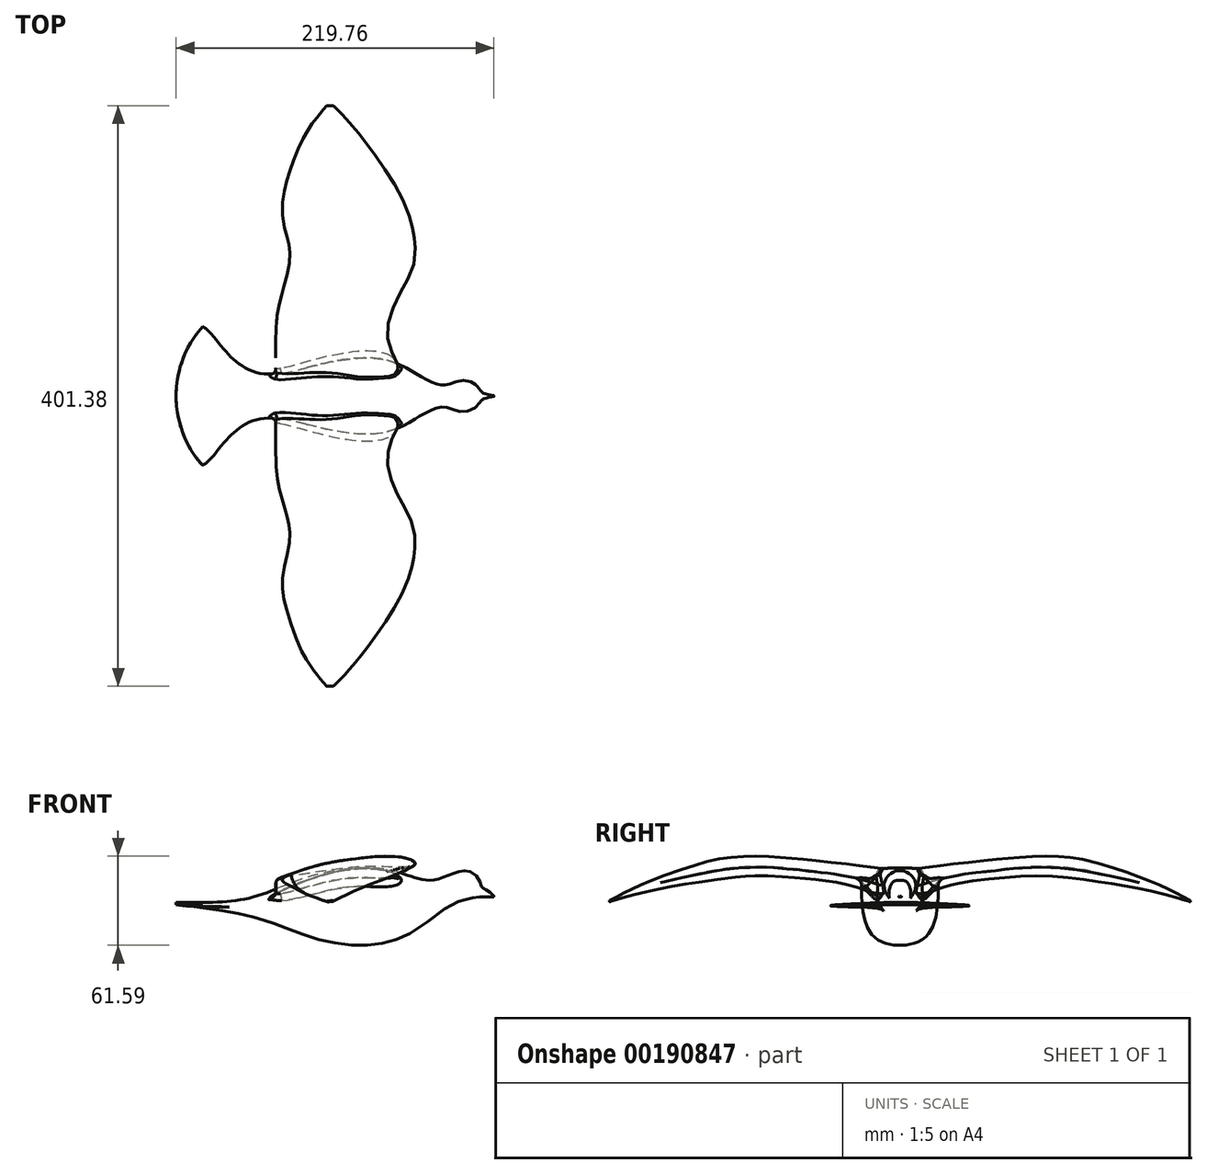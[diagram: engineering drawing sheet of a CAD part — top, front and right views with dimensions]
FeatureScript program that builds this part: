
annotation { "Feature Type Name" : "Feature", "Feature Type Description" : "" }
export const myFeature = defineFeature(function(context is Context, id is Id, definition is map)
    precondition{}
    {
        {
            var Q0;
            Q0=qCreatedBy(makeId("Front.planeOp"),FACE);
            var sketch = newSketch(context, id + "F0", { "sketchPlane" : qUnion([Q0])});
            skFitSpline(sketch, "E0", {"points": [v(88.88, 8.24) * mm, v(81.16, 14.04) * mm, v(79.82, 15.6) * mm, v(77.74, 20.52) * mm, v(69.16, 26.32) * mm, v(49.8, 20.45) * mm, v(34.16, 21.33) * mm, v(13, 27.34) * mm, v(-24.47, 25.74) * mm, v(-55.86, 16.14) * mm, v(-89.32, 5.77) * mm, v(-146.84, 4.8) * mm], "startDerivative": vector(-94.93, 149.18) * mm, "endDerivative": vector(-242.05, 4.9) * mm});
            skFitSpline(sketch, "E1", {"points": [v(-146.84, 4.8) * mm, v(-98.32, -1.47) * mm, v(-63.3, -10.47) * mm, v(-28.78, -22.29) * mm, v(10.92, -24.11) * mm, v(36.51, -13.67) * mm, v(49.57, -3.48) * mm, v(62.2, 4.2) * mm, v(74.07, 7.48) * mm, v(79.66, 8.19) * mm, v(88.88, 8.24) * mm], "startDerivative": vector(194.97, -32.1) * mm, "endDerivative": vector(155.18, 5.35) * mm});
            skLineSegment(sketch, "E2", {"start": v(78.61, 8.13) * mm, "end": v(80.27, 14.79) * mm, "construction": true});
            skLineSegment(sketch, "E3", {"start": v(70.02, 6.63) * mm, "end": v(70.7, 26.08) * mm, "construction": true});
            skLineSegment(sketch, "E4", {"start": v(58.33, 2.37) * mm, "end": v(51.98, 21.1) * mm, "construction": true});
            skLineSegment(sketch, "E5", {"start": v(29.9, -17.56) * mm, "end": v(25.63, 24.14) * mm, "construction": true});
            skLineSegment(sketch, "E6", {"start": v(-8, -25.25) * mm, "end": v(-11.3, 27.63) * mm, "construction": true});
            skLineSegment(sketch, "E7", {"start": v(-48.68, -15.99) * mm, "end": v(-48.68, 18.9) * mm, "construction": true});
            skLineSegment(sketch, "E8", {"start": v(-78.1, -5.74) * mm, "end": v(-78.1, 8.02) * mm, "construction": true});
            skLineSegment(sketch, "E9", {"start": v(-99.16, -1.33) * mm, "end": v(-99.57, 4.76) * mm, "construction": true});
            skLineSegment(sketch, "E10", {"start": v(88.2, 8.22) * mm, "end": v(88.46, 8.84) * mm});
            skLineSegment(sketch, "E11", {"start": v(-133.72, 3.08) * mm, "end": v(-133.72, 4.45) * mm});
            skLineSegment(sketch, "E12", {"start": v(-116.16, 4.23) * mm, "end": v(-116.16, 1) * mm, "construction": true});
            skLineSegment(sketch, "E13", {"start": v(-137.67, 4.56) * mm, "end": v(-133.72, 4.45) * mm});
            skLineSegment(sketch, "E14", {"start": v(-137.8, 3.61) * mm, "end": v(-133.72, 3.08) * mm});
            skLineSegment(sketch, "E15", {"start": v(-137.67, 4.56) * mm, "end": v(-137.8, 3.61) * mm});
            skSolve(sketch);
        }
        {
            var Q0;
            Q0=sQuery(id+"F0.wireOp",EDGE,"E10");
            cPlane(context, id + "F1", {"entities" : qUnion([Q0]), "cplaneType" : CPlaneType.LINE_ANGLE, "offset" : 25 * mm, "angle" : 0 * degree, "width" : 150 * mm, "height" : 150 * mm});
        }
        {
            var Q0;
            Q0=qCreatedBy(id+"F1.planeOp",FACE);
            var sketch = newSketch(context, id + "F2", { "sketchPlane" : qUnion([Q0])});
            skPoint(sketch, "E16.0", {"position": v(0, 41.6) * mm});
            skFitSpline(sketch, "E17", {"points": [v(0, 41.93) * mm, v(-0.33, 41.79) * mm, v(-0.34, 41.48) * mm, v(0, 41.26) * mm], "startDerivative": vector(-1.4, 0) * mm, "endDerivative": vector(1.32, 0) * mm});
            skFitSpline(sketch, "E18.MirrorCS", {"points": [v(0, 41.93) * mm, v(0.33, 41.79) * mm, v(0.34, 41.48) * mm, v(0, 41.26) * mm], "startDerivative": vector(1.4, 0) * mm, "endDerivative": vector(-1.32, 0) * mm});
            skSolve(sketch);
        }
        {
            var Q0;
            Q0=sQuery(id+"F0.wireOp",EDGE,"E2");
            cPlane(context, id + "F3", {"entities" : qUnion([Q0]), "cplaneType" : CPlaneType.LINE_ANGLE, "offset" : 25 * mm, "angle" : 0 * degree, "width" : 150 * mm, "height" : 150 * mm});
        }
        {
            var Q0;
            Q0=qCreatedBy(id+"F3.planeOp",FACE);
            var sketch = newSketch(context, id + "F4", { "sketchPlane" : qUnion([Q0])});
            skFitSpline(sketch, "E19", {"points": [v(0, 33.77) * mm, v(-2.62, 32.5) * mm, v(-2.94, 28.5) * mm, v(0, 26.91) * mm], "startDerivative": vector(-11.48, 0) * mm, "endDerivative": vector(10.21, 0) * mm});
            skFitSpline(sketch, "E20.MirrorCS", {"points": [v(0, 33.77) * mm, v(2.62, 32.5) * mm, v(2.94, 28.5) * mm, v(0, 26.91) * mm], "startDerivative": vector(11.48, 0) * mm, "endDerivative": vector(-10.21, 0) * mm});
            skSolve(sketch);
        }
        {
            var Q0;
            Q0=sQuery(id+"F0.wireOp",EDGE,"E3");
            cPlane(context, id + "F5", {"entities" : qUnion([Q0]), "cplaneType" : CPlaneType.LINE_ANGLE, "offset" : 25 * mm, "angle" : 0 * degree, "width" : 150 * mm, "height" : 150 * mm});
        }
        {
            var Q0;
            Q0=qCreatedBy(id+"F5.planeOp",FACE);
            var sketch = newSketch(context, id + "F6", { "sketchPlane" : qUnion([Q0])});
            skFitSpline(sketch, "E21", {"points": [v(0, 28.5) * mm, v(-9.3, 23.37) * mm, v(-8.68, 12.9) * mm, v(0, 9.03) * mm], "startDerivative": vector(-26.88, 0) * mm, "endDerivative": vector(31.08, 0) * mm});
            skFitSpline(sketch, "E22.MirrorCS", {"points": [v(0, 28.5) * mm, v(9.3, 23.37) * mm, v(8.68, 12.9) * mm, v(0, 9.03) * mm], "startDerivative": vector(26.88, 0) * mm, "endDerivative": vector(-31.08, 0) * mm});
            skSolve(sketch);
        }
        {
            var Q0;
            Q0=sQuery(id+"F0.wireOp",EDGE,"E4");
            cPlane(context, id + "F7", {"entities" : qUnion([Q0]), "cplaneType" : CPlaneType.LINE_ANGLE, "offset" : 25 * mm, "angle" : 0 * degree, "width" : 150 * mm, "height" : 150 * mm});
        }
        {
            var Q0;
            Q0=qCreatedBy(id+"F7.planeOp",FACE);
            var sketch = newSketch(context, id + "F8", { "sketchPlane" : qUnion([Q0])});
            skFitSpline(sketch, "E23", {"points": [v(0, 3.3) * mm, v(-6.8, -1.95) * mm, v(-7.06, -11.7) * mm, v(0, -16.48) * mm], "startDerivative": vector(-36.57, 0) * mm, "endDerivative": vector(34.27, 0) * mm});
            skFitSpline(sketch, "E24.MirrorCS", {"points": [v(0, 3.3) * mm, v(6.8, -1.95) * mm, v(7.06, -11.7) * mm, v(0, -16.48) * mm], "startDerivative": vector(36.57, 0) * mm, "endDerivative": vector(-34.27, 0) * mm});
            skSolve(sketch);
        }
        {
            var Q0;
            Q0=sQuery(id+"F0.wireOp",EDGE,"E5");
            cPlane(context, id + "F9", {"entities" : qUnion([Q0]), "cplaneType" : CPlaneType.LINE_ANGLE, "offset" : 25 * mm, "angle" : 0 * degree, "width" : 150 * mm, "height" : 150 * mm});
        }
        {
            var Q0;
            Q0=qCreatedBy(id+"F9.planeOp",FACE);
            var sketch = newSketch(context, id + "F10", { "sketchPlane" : qUnion([Q0])});
            skFitSpline(sketch, "E25", {"points": [v(0, 21.4) * mm, v(-14.3, 18.7) * mm, v(-19.1, 14.04) * mm, v(-15, -12.2) * mm, v(0, -20.5) * mm], "startDerivative": vector(-90.7, 0) * mm, "endDerivative": vector(69.38, 0) * mm});
            skFitSpline(sketch, "E26.MirrorCS", {"points": [v(0, 21.4) * mm, v(14.3, 18.7) * mm, v(19.1, 14.04) * mm, v(15, -12.2) * mm, v(0, -20.5) * mm], "startDerivative": vector(90.7, 0) * mm, "endDerivative": vector(-69.38, 0) * mm});
            skSolve(sketch);
        }
        {
            var Q0;
            Q0=sQuery(id+"F0.wireOp",EDGE,"E6");
            cPlane(context, id + "F11", {"entities" : qUnion([Q0]), "cplaneType" : CPlaneType.LINE_ANGLE, "offset" : 25 * mm, "angle" : 0 * degree, "width" : 150 * mm, "height" : 150 * mm});
        }
        {
            var Q0;
            Q0=qCreatedBy(id+"F11.planeOp",FACE);
            var sketch = newSketch(context, id + "F12", { "sketchPlane" : qUnion([Q0])});
            skFitSpline(sketch, "E27", {"points": [v(0, 28.28) * mm, v(-20, 26.45) * mm, v(-24.93, 24.12) * mm, v(-25.49, 20.68) * mm, v(-21, -15.24) * mm, v(0, -24.7) * mm], "startDerivative": vector(-91.64, 0) * mm, "endDerivative": vector(71.43, 0) * mm});
            skFitSpline(sketch, "E28.MirrorCS", {"points": [v(0, 28.28) * mm, v(20, 26.45) * mm, v(24.93, 24.12) * mm, v(25.49, 20.68) * mm, v(21, -15.24) * mm, v(0, -24.7) * mm], "startDerivative": vector(91.64, 0) * mm, "endDerivative": vector(-71.43, 0) * mm});
            skSolve(sketch);
        }
        {
            var Q0;
            Q0=sQuery(id+"F0.wireOp",EDGE,"E7");
            cPlane(context, id + "F13", {"entities" : qUnion([Q0]), "cplaneType" : CPlaneType.LINE_ANGLE, "offset" : 25 * mm, "angle" : 0 * degree, "width" : 150 * mm, "height" : 150 * mm});
        }
        {
            var Q0;
            Q0=qCreatedBy(id+"F13.planeOp",FACE);
            var sketch = newSketch(context, id + "F14", { "sketchPlane" : qUnion([Q0])});
            skFitSpline(sketch, "E29", {"points": [v(0, 18.9) * mm, v(-14, 16.03) * mm, v(-17.48, 14.36) * mm, v(-17.75, 10.54) * mm, v(-13.32, -9.87) * mm, v(0, -15.99) * mm], "startDerivative": vector(-44.92, 0) * mm, "endDerivative": vector(32.23, 0) * mm});
            skFitSpline(sketch, "E30.MirrorCS", {"points": [v(0, 18.9) * mm, v(14, 16.03) * mm, v(17.48, 14.36) * mm, v(17.75, 10.54) * mm, v(13.32, -9.87) * mm, v(0, -15.99) * mm], "startDerivative": vector(44.92, 0) * mm, "endDerivative": vector(-32.23, 0) * mm});
            skSolve(sketch);
        }
        {
            var Q0;
            Q0=sQuery(id+"F0.wireOp",EDGE,"E8");
            cPlane(context, id + "F15", {"entities" : qUnion([Q0]), "cplaneType" : CPlaneType.LINE_ANGLE, "offset" : 25 * mm, "angle" : 0 * degree, "width" : 150 * mm, "height" : 150 * mm});
        }
        {
            var Q0;
            Q0=qCreatedBy(id+"F15.planeOp",FACE);
            var sketch = newSketch(context, id + "F16", { "sketchPlane" : qUnion([Q0])});
            skFitSpline(sketch, "E31.MirrorCS", {"points": [v(0, 8.02) * mm, v(12.6, 5.46) * mm, v(17.04, 3.17) * mm, v(12.95, -0.34) * mm, v(0, -5.74) * mm], "startDerivative": vector(27.61, 0) * mm, "endDerivative": vector(-43.83, 0) * mm});
            skFitSpline(sketch, "E32.MirrorCS", {"points": [v(0, 8.02) * mm, v(-12.6, 5.46) * mm, v(-17.04, 3.17) * mm, v(-12.95, -0.34) * mm, v(0, -5.74) * mm], "startDerivative": vector(-27.61, 0) * mm, "endDerivative": vector(43.83, 0) * mm});
            skSolve(sketch);
        }
        {
            var Q0;
            Q0=sQuery(id+"F0.wireOp",EDGE,"E9");
            cPlane(context, id + "F17", {"entities" : qUnion([Q0]), "cplaneType" : CPlaneType.LINE_ANGLE, "offset" : 25 * mm, "angle" : 0 * degree, "width" : 150 * mm, "height" : 150 * mm});
        }
        {
            var Q0;
            Q0=qCreatedBy(id+"F17.planeOp",FACE);
            var sketch = newSketch(context, id + "F18", { "sketchPlane" : qUnion([Q0])});
            skFitSpline(sketch, "E33", {"points": [v(0, 11.5) * mm, v(-13.03, 10.57) * mm, v(-30.8, 9.85) * mm, v(-32.65, 9.42) * mm, v(-33.6, 8.68) * mm, v(-32.69, 8.15) * mm, v(-30.62, 7.89) * mm, v(-12.76, 7.68) * mm, v(0, 5.4) * mm], "startDerivative": vector(-51.31, 0) * mm, "endDerivative": vector(35.96, 0) * mm});
            skFitSpline(sketch, "E34.MirrorCS", {"points": [v(0, 11.5) * mm, v(13.03, 10.57) * mm, v(30.8, 9.85) * mm, v(32.65, 9.42) * mm, v(33.6, 8.68) * mm, v(32.69, 8.15) * mm, v(30.62, 7.89) * mm, v(12.76, 7.68) * mm, v(0, 5.4) * mm], "startDerivative": vector(51.31, 0) * mm, "endDerivative": vector(-35.96, 0) * mm});
            skSolve(sketch);
        }
        {
            var Q0;
            Q0=sQuery(id+"F0.wireOp",EDGE,"E12");
            cPlane(context, id + "F19", {"entities" : qUnion([Q0]), "cplaneType" : CPlaneType.LINE_ANGLE, "offset" : 25 * mm, "angle" : 0 * degree, "width" : 150 * mm, "height" : 150 * mm});
        }
        {
            var Q0;
            Q0=qCreatedBy(id+"F19.planeOp",FACE);
            var sketch = newSketch(context, id + "F20", { "sketchPlane" : qUnion([Q0])});
            skFitSpline(sketch, "E35", {"points": [v(0, 4.23) * mm, v(19.93, 3.75) * mm, v(36.27, 3.06) * mm, v(48.32, 2.16) * mm, v(36.04, 1.6) * mm, v(17.82, 1.4) * mm, v(0, 1) * mm], "startDerivative": vector(87.2, 0) * mm, "endDerivative": vector(-89.38, 0) * mm});
            skFitSpline(sketch, "E36.MirrorCS", {"points": [v(0, 4.23) * mm, v(-19.93, 3.75) * mm, v(-36.27, 3.06) * mm, v(-48.32, 2.16) * mm, v(-36.04, 1.6) * mm, v(-17.82, 1.4) * mm, v(0, 1) * mm], "startDerivative": vector(-87.2, 0) * mm, "endDerivative": vector(89.38, 0) * mm});
            skSolve(sketch);
        }
        {
            var Q0;
            Q0=sQuery(id+"F0.wireOp",EDGE,"E11");
            cPlane(context, id + "F21", {"entities" : qUnion([Q0]), "cplaneType" : CPlaneType.LINE_ANGLE, "offset" : 25 * mm, "angle" : 0 * degree, "width" : 150 * mm, "height" : 150 * mm});
        }
        {
            var Q0;
            Q0=qCreatedBy(id+"F21.planeOp",FACE);
            var sketch = newSketch(context, id + "F22", { "sketchPlane" : qUnion([Q0])});
            skFitSpline(sketch, "E37", {"points": [v(0, 4.45) * mm, v(-6.92, 4.3) * mm, v(-10.95, 3.97) * mm, v(-12.2, 3.75) * mm, v(-12.37, 3.62) * mm, v(-12.11, 3.48) * mm, v(-10.98, 3.35) * mm, v(-6.9, 3.2) * mm, v(0, 3.08) * mm], "startDerivative": vector(-30.72, 0) * mm, "endDerivative": vector(29.33, 0.08) * mm});
            skFitSpline(sketch, "E38.MirrorCS", {"points": [v(0, 4.45) * mm, v(6.92, 4.3) * mm, v(10.95, 3.97) * mm, v(12.2, 3.75) * mm, v(12.37, 3.62) * mm, v(12.11, 3.48) * mm, v(10.98, 3.35) * mm, v(6.9, 3.2) * mm, v(0, 3.08) * mm], "startDerivative": vector(30.72, 0) * mm, "endDerivative": vector(-29.33, 0.08) * mm});
            skSolve(sketch);
        }
        {
            var Q0;
            Q0=sQuery(id+"F0.wireOp",EDGE,"E15");
            cPlane(context, id + "F23", {"entities" : qUnion([Q0]), "cplaneType" : CPlaneType.LINE_ANGLE, "offset" : 25 * mm, "angle" : 0 * degree, "width" : 150 * mm, "height" : 150 * mm});
        }
        {
            var Q0;
            Q0=makeQuery(id+"F2.imprint","IMPRINT",FACE,{"disambiguationData":[TD([[makeQuery(id+"F2.imprint","IMPRINT",EDGE,{"derivedFrom":sQuery(id+"F2.wireOp",EDGE,"E17")}),1.0]])]});
            var Q1;
            Q1=makeQuery(id+"F4.imprint","IMPRINT",FACE,{"disambiguationData":[TD([[makeQuery(id+"F4.imprint","IMPRINT",EDGE,{"derivedFrom":sQuery(id+"F4.wireOp",EDGE,"E19")}),1.0]])]});
            var Q2;
            Q2=makeQuery(id+"F6.imprint","IMPRINT",FACE,{"disambiguationData":[TD([[makeQuery(id+"F6.imprint","IMPRINT",EDGE,{"derivedFrom":sQuery(id+"F6.wireOp",EDGE,"E21")}),1.0]])]});
            var Q3;
            Q3=makeQuery(id+"F8.imprint","IMPRINT",FACE,{"disambiguationData":[TD([[makeQuery(id+"F8.imprint","IMPRINT",EDGE,{"derivedFrom":sQuery(id+"F8.wireOp",EDGE,"E23")}),1.0]])]});
            var Q4;
            Q4=makeQuery(id+"F10.imprint","IMPRINT",FACE,{"disambiguationData":[TD([[makeQuery(id+"F10.imprint","IMPRINT",EDGE,{"derivedFrom":sQuery(id+"F10.wireOp",EDGE,"E25")}),1.0]])]});
            var Q5;
            Q5=makeQuery(id+"F12.imprint","IMPRINT",FACE,{"disambiguationData":[TD([[makeQuery(id+"F12.imprint","IMPRINT",EDGE,{"derivedFrom":sQuery(id+"F12.wireOp",EDGE,"E27")}),1.0]])]});
            var Q6;
            Q6=makeQuery(id+"F14.imprint","IMPRINT",FACE,{"disambiguationData":[TD([[makeQuery(id+"F14.imprint","IMPRINT",EDGE,{"derivedFrom":sQuery(id+"F14.wireOp",EDGE,"E29")}),1.0]])]});
            var Q7;
            Q7=makeQuery(id+"F16.imprint","IMPRINT",FACE,{"disambiguationData":[TD([[makeQuery(id+"F16.imprint","IMPRINT",EDGE,{"derivedFrom":sQuery(id+"F16.wireOp",EDGE,"E31.MirrorCS")}),-1.0]])]});
            var Q8;
            Q8=makeQuery(id+"F18.imprint","IMPRINT",FACE,{"disambiguationData":[TD([[makeQuery(id+"F18.imprint","IMPRINT",EDGE,{"derivedFrom":sQuery(id+"F18.wireOp",EDGE,"E33")}),1.0]])]});
            var Q9;
            Q9=makeQuery(id+"F20.imprint","IMPRINT",FACE,{"disambiguationData":[TD([[makeQuery(id+"F20.imprint","IMPRINT",EDGE,{"derivedFrom":sQuery(id+"F20.wireOp",EDGE,"E35")}),-1.0]])]});
            var Q10;
            Q10=makeQuery(id+"F22.imprint","IMPRINT",FACE,{"disambiguationData":[TD([[makeQuery(id+"F22.imprint","IMPRINT",EDGE,{"derivedFrom":sQuery(id+"F22.wireOp",EDGE,"E37")}),1.0]])]});
            var Q11;
            Q11=sQuery(id+"F0.wireOp",EDGE,"E0");
            var Q12;
            Q12=sQuery(id+"F0.wireOp",EDGE,"E1");
            loft(context, id + "F24", {"addGuides" : true, "sheetProfilesArray" : [{ "sheetProfileEntities" : qUnion([Q0]) }, { "sheetProfileEntities" : qUnion([Q1]) }, { "sheetProfileEntities" : qUnion([Q2]) }, { "sheetProfileEntities" : qUnion([Q3]) }, { "sheetProfileEntities" : qUnion([Q4]) }, { "sheetProfileEntities" : qUnion([Q5]) }, { "sheetProfileEntities" : qUnion([Q6]) }, { "sheetProfileEntities" : qUnion([Q7]) }, { "sheetProfileEntities" : qUnion([Q8]) }, { "sheetProfileEntities" : qUnion([Q9]) }, { "sheetProfileEntities" : qUnion([Q10]) }], "guidesArray" : [{ "guideEntities" : qUnion([Q11]), "guideDerivativeType" : LoftGuideDerivativeType.DEFAULT, "guideDerivativeMagnitude" : 1 }, { "guideEntities" : qUnion([Q12]), "guideDerivativeType" : LoftGuideDerivativeType.DEFAULT, "guideDerivativeMagnitude" : 1 }]});
        }
        {
            var Q0;
            Q0=qCreatedBy(makeId("Top.planeOp"),FACE);
            var sketch = newSketch(context, id + "F25", { "sketchPlane" : qUnion([Q0])});
            skFitSpline(sketch, "E39.0", {"points": [v(88.88, 0) * mm, v(86.77, 0) * mm, v(81.02, 0) * mm, v(79.63, 0) * mm, v(78.28, 0) * mm, v(68.93, 0) * mm, v(49.66, 0) * mm, v(33.6, 0) * mm, v(12.87, 0) * mm, v(-25.59, 0) * mm, v(-55.45, 0) * mm, v(-88.82, 0) * mm, v(-110.43, 0) * mm, v(-120.23, 0) * mm]});
            skFitSpline(sketch, "E40", {"points": [v(26.18, -8.4) * mm, v(17.96, -38.7) * mm, v(22.3, -68.14) * mm, v(33.97, -89.37) * mm, v(36.14, -111.88) * mm, v(24.45, -140.9) * mm, v(-13.24, -194.17) * mm, v(-26.66, -200.64) * mm, v(-34.87, -196.33) * mm, v(-43.97, -184.2) * mm, v(-54.36, -163.85) * mm, v(-62.6, -133.54) * mm, v(-58.26, -96.29) * mm, v(-56.13, -82.45) * mm, v(-59.13, -64.25) * mm, v(-60, -43.9) * mm, v(-57.17, -26.76) * mm, v(-57.83, -10.98) * mm], "startDerivative": vector(-232.8, -442.21) * mm, "endDerivative": vector(-41.43, 614.06) * mm});
            skSolve(sketch);
        }
        {
            var Q0;
            Q0=qCreatedBy(makeId("Front.planeOp"),FACE);
            cPlane(context, id + "F26", {"entities" : qUnion([Q0]), "cplaneType" : CPlaneType.OFFSET, "offset" : 30 * mm, "width" : 150 * mm, "height" : 150 * mm});
        }
        {
            var Q0;
            Q0=qCreatedBy(id+"F26.planeOp",FACE);
            cPlane(context, id + "F27", {"entities" : qUnion([Q0]), "cplaneType" : CPlaneType.OFFSET, "offset" : 30 * mm, "width" : 150 * mm, "height" : 150 * mm});
        }
        {
            var Q0;
            Q0=qCreatedBy(id+"F27.planeOp",FACE);
            cPlane(context, id + "F28", {"entities" : qUnion([Q0]), "cplaneType" : CPlaneType.OFFSET, "offset" : 30 * mm, "width" : 150 * mm, "height" : 150 * mm});
        }
        {
            var Q0;
            Q0=qCreatedBy(id+"F28.planeOp",FACE);
            cPlane(context, id + "F29", {"entities" : qUnion([Q0]), "cplaneType" : CPlaneType.OFFSET, "offset" : 30 * mm, "width" : 150 * mm, "height" : 150 * mm});
        }
        {
            var Q0;
            Q0=qCreatedBy(id+"F29.planeOp",FACE);
            cPlane(context, id + "F30", {"entities" : qUnion([Q0]), "cplaneType" : CPlaneType.OFFSET, "offset" : 30 * mm, "width" : 150 * mm, "height" : 150 * mm});
        }
        {
            var Q0;
            Q0=qCreatedBy(id+"F30.planeOp",FACE);
            cPlane(context, id + "F31", {"entities" : qUnion([Q0]), "cplaneType" : CPlaneType.OFFSET, "offset" : 30 * mm, "width" : 150 * mm, "height" : 150 * mm});
        }
        {
            var Q0;
            Q0=qCreatedBy(makeId("Right.planeOp"),FACE);
            cPlane(context, id + "F32", {"entities" : qUnion([Q0]), "cplaneType" : CPlaneType.OFFSET, "offset" : 25 * mm, "oppositeDirection" : true, "width" : 150 * mm, "height" : 150 * mm});
        }
        {
            var Q0;
            Q0=qCreatedBy(id+"F32.planeOp",FACE);
            var sketch = newSketch(context, id + "F33", { "sketchPlane" : qUnion([Q0])});
            skFitSpline(sketch, "E41.0", {"points": [v(-8.4, 0) * mm, v(-72.5, 0) * mm, v(-136.6, 0) * mm, v(-200.7, 0) * mm]});
            skFitSpline(sketch, "E42", {"points": [v(0, 17.32) * mm, v(-40.84, 25.14) * mm, v(-90.53, 29.84) * mm, v(-139.25, 25.73) * mm, v(-180.53, 16.73) * mm, v(-200.7, 10.1) * mm], "startDerivative": vector(-193.81, 40.58) * mm, "endDerivative": vector(-128.78, -46.17) * mm});
            skLineSegment(sketch, "E43", {"start": v(-29.69, 11.76) * mm, "end": v(-135.12, 11.76) * mm, "construction": true});
            skSolve(sketch);
        }
        {
            var Q0;
            Q0=qCreatedBy(makeId("Front.planeOp"),FACE);
            var sketch = newSketch(context, id + "F34", { "sketchPlane" : qUnion([Q0])});
            skFitSpline(sketch, "E44", {"points": [v(-64.04, 9.17) * mm, v(-28.08, 22.51) * mm, v(12.48, 28.75) * mm, v(31.83, 22.4) * mm, v(37.03, 16.44) * mm, v(37.26, 13.2) * mm, v(34.73, 12.47) * mm, v(14.83, 13.48) * mm, v(-17.47, 13.56) * mm, v(-64.03, 6.62) * mm, v(-64.94, 7.7) * mm, v(-64.04, 9.17) * mm]});
            skSolve(sketch);
        }
        {
            var Q0;
            Q0=qCreatedBy(id+"F26.planeOp",FACE);
            var sketch = newSketch(context, id + "F35", { "sketchPlane" : qUnion([Q0])});
            skLineSegment(sketch, "E45", {"start": v(18.9, 0) * mm, "end": v(18.9, 25.28) * mm, "construction": true});
            skLineSegment(sketch, "E46", {"start": v(-57.68, 0) * mm, "end": v(-57.68, 26.94) * mm, "construction": true});
            skLineSegment(sketch, "E47", {"start": v(-25, 23.3) * mm, "end": v(18.9, 23.3) * mm, "construction": true});
            skLineSegment(sketch, "E48", {"start": v(-25, 23.3) * mm, "end": v(-61.85, 23.3) * mm, "construction": true});
            skFitSpline(sketch, "E49", {"points": [v(-61.85, 23.04) * mm, v(-61.67, 23.52) * mm, v(-36.6, 30.43) * mm, v(-10.14, 33.81) * mm, v(10.55, 31.1) * mm, v(17.62, 27.06) * mm, v(18.9, 24.93) * mm, v(17.05, 23.93) * mm, v(9.12, 23.64) * mm, v(-6.85, 24.93) * mm, v(-32.78, 24.08) * mm, v(-61.46, 22.53) * mm, v(-61.85, 23.04) * mm]});
            skSolve(sketch);
        }
        {
            var Q0;
            Q0=qCreatedBy(id+"F27.planeOp",FACE);
            var sketch = newSketch(context, id + "F36", { "sketchPlane" : qUnion([Q0])});
            skLineSegment(sketch, "E50", {"start": v(19.64, 0) * mm, "end": v(19.64, 27.8) * mm, "construction": true});
            skLineSegment(sketch, "E51", {"start": v(-59.75, 0) * mm, "end": v(-59.75, 27.8) * mm, "construction": true});
            skLineSegment(sketch, "E52", {"start": v(-25, 27.8) * mm, "end": v(19.64, 27.8) * mm, "construction": true});
            skLineSegment(sketch, "E53", {"start": v(-25, 27.8) * mm, "end": v(-59.75, 27.8) * mm, "construction": true});
            skLineSegment(sketch, "E54", {"start": v(19.64, 27.8) * mm, "end": v(19.64, 29.9) * mm, "construction": true});
            skFitSpline(sketch, "E55", {"points": [v(-59.75, 27.8) * mm, v(-36.09, 33.52) * mm, v(-9.47, 37.07) * mm, v(10.01, 35.3) * mm, v(17.74, 32.2) * mm, v(19.64, 29.9) * mm, v(19.2, 28.69) * mm, v(17.15, 28.08) * mm, v(9, 28.31) * mm, v(-3.67, 29.65) * mm, v(-24.5, 30.23) * mm, v(-40.61, 29.18) * mm, v(-59.75, 27.8) * mm]});
            skSolve(sketch);
        }
        {
            var Q0;
            Q0=qCreatedBy(id+"F28.planeOp",FACE);
            var sketch = newSketch(context, id + "F37", { "sketchPlane" : qUnion([Q0])});
            skLineSegment(sketch, "E56", {"start": v(34.22, 0) * mm, "end": v(34.22, 31.71) * mm, "construction": true});
            skLineSegment(sketch, "E57", {"start": v(-56.85, 0) * mm, "end": v(-56.85, 29.83) * mm, "construction": true});
            skLineSegment(sketch, "E58", {"start": v(-25, 29.83) * mm, "end": v(34.22, 29.83) * mm, "construction": true});
            skLineSegment(sketch, "E59", {"start": v(-25, 29.83) * mm, "end": v(-56.85, 29.83) * mm, "construction": true});
            skFitSpline(sketch, "E60", {"points": [v(-52.03, 29.83) * mm, v(-33.28, 35.12) * mm, v(-5.58, 38.16) * mm, v(16.12, 38.09) * mm, v(32.25, 34.32) * mm, v(34.22, 31.71) * mm, v(33.47, 30.57) * mm, v(21.96, 30.18) * mm, v(3.32, 32.01) * mm, v(-32.78, 30.85) * mm, v(-52.03, 29.83) * mm]});
            skSolve(sketch);
        }
        {
            var Q0;
            Q0=qCreatedBy(id+"F29.planeOp",FACE);
            var sketch = newSketch(context, id + "F38", { "sketchPlane" : qUnion([Q0])});
            skLineSegment(sketch, "E61", {"start": v(34.24, 0) * mm, "end": v(34.24, 30.7) * mm, "construction": true});
            skLineSegment(sketch, "E62", {"start": v(-62.23, 0) * mm, "end": v(-62.23, 28.36) * mm, "construction": true});
            skLineSegment(sketch, "E63", {"start": v(-25, 28.36) * mm, "end": v(34.24, 28.36) * mm, "construction": true});
            skLineSegment(sketch, "E64", {"start": v(-25, 28.36) * mm, "end": v(-62.23, 28.36) * mm, "construction": true});
            skFitSpline(sketch, "E65", {"points": [v(-55.98, 28.36) * mm, v(-35.1, 34.06) * mm, v(-3.18, 37.42) * mm, v(18.24, 37.07) * mm, v(30.03, 33.69) * mm, v(32.7, 30.66) * mm, v(31.49, 29.24) * mm, v(22.41, 28.94) * mm, v(3.31, 31.05) * mm, v(-33.8, 29.97) * mm, v(-55.98, 28.36) * mm]});
            skSolve(sketch);
        }
        {
            var Q0;
            Q0=qCreatedBy(id+"F30.planeOp",FACE);
            var sketch = newSketch(context, id + "F39", { "sketchPlane" : qUnion([Q0])});
            skLineSegment(sketch, "E66", {"start": v(19.1, 0) * mm, "end": v(19.1, 25.28) * mm, "construction": true});
            skLineSegment(sketch, "E67", {"start": v(-59.63, 0) * mm, "end": v(-59.63, 23.56) * mm, "construction": true});
            skLineSegment(sketch, "E68", {"start": v(-25, 23.81) * mm, "end": v(19.1, 23.81) * mm, "construction": true});
            skLineSegment(sketch, "E69", {"start": v(-25, 23.81) * mm, "end": v(-57.17, 23.81) * mm, "construction": true});
            skFitSpline(sketch, "E70", {"points": [v(-53.58, 23.81) * mm, v(-40.8, 27.9) * mm, v(-12.84, 30.8) * mm, v(10.13, 29.68) * mm, v(17.13, 26.99) * mm, v(18.4, 24.61) * mm, v(16.41, 23.82) * mm, v(0.26, 25.08) * mm, v(-19.78, 25.63) * mm, v(-40.95, 24.47) * mm, v(-53.58, 23.81) * mm]});
            skSolve(sketch);
        }
        {
            var Q0;
            Q0=qCreatedBy(id+"F31.planeOp",FACE);
            var sketch = newSketch(context, id + "F40", { "sketchPlane" : qUnion([Q0])});
            skLineSegment(sketch, "E71", {"start": v(-1.01, 0) * mm, "end": v(-1.01, 16.88) * mm, "construction": true});
            skLineSegment(sketch, "E72", {"start": v(-46.4, 0) * mm, "end": v(-46.4, 16.83) * mm, "construction": true});
            skLineSegment(sketch, "E73", {"start": v(-25, 16.88) * mm, "end": v(-1.01, 16.88) * mm, "construction": true});
            skLineSegment(sketch, "E74", {"start": v(-25, 16.88) * mm, "end": v(-45.16, 16.88) * mm, "construction": true});
            skFitSpline(sketch, "E75", {"points": [v(-42.27, 16.88) * mm, v(-34.5, 18.85) * mm, v(-18.32, 20.43) * mm, v(-5.9, 19.1) * mm, v(-3.36, 17.64) * mm, v(-7.67, 17.22) * mm, v(-13.43, 17.46) * mm, v(-28.7, 17.44) * mm, v(-42.27, 16.88) * mm]});
            skSolve(sketch);
        }
        {
            var Q0;
            Q0=makeQuery(id+"F40.imprint","IMPRINT",FACE,{"disambiguationData":[TD([[makeQuery(id+"F40.imprint","IMPRINT",EDGE,{"derivedFrom":sQuery(id+"F40.wireOp",EDGE,"E75")}),-1.0]])]});
            var Q1;
            Q1=sQuery(id+"F33.wireOp",VERTEX,"E42.end");
            cPlane(context, id + "F41", {"entities" : qUnion([Q0, Q1]), "cplaneType" : CPlaneType.PLANE_POINT, "offset" : 25 * mm, "width" : 150 * mm, "height" : 150 * mm});
        }
        {
            var Q0;
            Q0=qCreatedBy(id+"F41.planeOp",FACE);
            var sketch = newSketch(context, id + "F42", { "sketchPlane" : qUnion([Q0])});
            skPoint(sketch, "E76.0", {"position": v(-25, 10.1) * mm});
            skEllipse(sketch, "E77", {"center": v(-25, 10.1) * mm, "majorRadius": 2.5 * mm, "minorRadius": 0.3 * mm, "majorAxis": v(1, 0)});
            skSolve(sketch);
        }
        {
            var Q1;
            Q1 = qSketchRegion(id + "F34", true);
            var Q2;
            Q2 = qSketchRegion(id + "F35", true);
            var Q3;
            Q3 = qSketchRegion(id + "F36", true);
            var Q4;
            Q4 = qSketchRegion(id + "F37", true);
            var Q5;
            Q5 = qSketchRegion(id + "F38", true);
            var Q6;
            Q6 = qSketchRegion(id + "F39", true);
            var Q7;
            Q7 = qSketchRegion(id + "F40", true);
            var Q8;
            Q8=makeQuery(id+"F42.imprint","IMPRINT",FACE,{"disambiguationData":[TD([[makeQuery(id+"F42.imprint","IMPRINT",EDGE,{"derivedFrom":sQuery(id+"F42.wireOp",EDGE,"E77")}),1.0]])]});
            loft(context, id + "F43", {"sheetProfilesArray" : [{ "sheetProfileEntities" : qUnion([Q1]) }, { "sheetProfileEntities" : qUnion([Q2]) }, { "sheetProfileEntities" : qUnion([Q3]) }, { "sheetProfileEntities" : qUnion([Q4]) }, { "sheetProfileEntities" : qUnion([Q5]) }, { "sheetProfileEntities" : qUnion([Q6]) }, { "sheetProfileEntities" : qUnion([Q7]) }, { "sheetProfileEntities" : qUnion([Q8]) }]});
        }
        {
            var Q0;
            Q0=makeQuery(id+"F43.opLoft","SWEPT_BODY",BODY,{"disambiguationData":[OSD([makeQuery(id+"F34.imprint","IMPRINT",FACE,{"disambiguationData":[TD([[makeQuery(id+"F34.imprint","IMPRINT",EDGE,{"derivedFrom":sQuery(id+"F34.wireOp",EDGE,"E44")}),-1.0]])]}),sQuery(id+"F35.wireOp",EDGE,"E49"),sQuery(id+"F36.wireOp",EDGE,"E55"),sQuery(id+"F37.wireOp",EDGE,"E60"),sQuery(id+"F38.wireOp",EDGE,"E65"),sQuery(id+"F39.wireOp",EDGE,"E70"),sQuery(id+"F40.wireOp",EDGE,"E75"),makeQuery(id+"F42.imprint","IMPRINT",FACE,{"disambiguationData":[TD([[makeQuery(id+"F42.imprint","IMPRINT",EDGE,{"derivedFrom":sQuery(id+"F42.wireOp",EDGE,"E77")}),1.0]])]})])]});
            var Q1;
            Q1=sQuery(id+"F33.wireOp",EDGE,"E43");
            transform(context, id + "F44", {"entities" : qUnion([Q0]), "transformType" : TransformType.ROTATION, "transformAxis" : qUnion([Q1]), "angle" : 4 * degree, "makeCopy" : false});
        }
        {
            var Q0;
            Q0=makeQuery(id+"F43.opLoft","SWEPT_BODY",BODY,{"disambiguationData":[OSD([makeQuery(id+"F34.imprint","IMPRINT",FACE,{"disambiguationData":[TD([[makeQuery(id+"F34.imprint","IMPRINT",EDGE,{"derivedFrom":sQuery(id+"F34.wireOp",EDGE,"E44")}),-1.0]])]}),sQuery(id+"F35.wireOp",EDGE,"E49"),sQuery(id+"F36.wireOp",EDGE,"E55"),sQuery(id+"F37.wireOp",EDGE,"E60"),sQuery(id+"F38.wireOp",EDGE,"E65"),sQuery(id+"F39.wireOp",EDGE,"E70"),sQuery(id+"F40.wireOp",EDGE,"E75"),makeQuery(id+"F42.imprint","IMPRINT",FACE,{"disambiguationData":[TD([[makeQuery(id+"F42.imprint","IMPRINT",EDGE,{"derivedFrom":sQuery(id+"F42.wireOp",EDGE,"E77")}),1.0]])]})])]});
            var Q1;
            Q1=qCreatedBy(makeId("Top.planeOp"),FACE);
            transform(context, id + "F45", {"entities" : qUnion([Q0]), "transformType" : TransformType.TRANSLATION_DISTANCE, "transformDirection" : qUnion([Q1]), "distance" : 5 * mm, "oppositeDirection" : true, "makeCopy" : false});
        }
        {
            var Q0;
            Q0=makeQuery(id+"F43.opLoft","SWEPT_BODY",BODY,{"disambiguationData":[OSD([makeQuery(id+"F34.imprint","IMPRINT",FACE,{"disambiguationData":[TD([[makeQuery(id+"F34.imprint","IMPRINT",EDGE,{"derivedFrom":sQuery(id+"F34.wireOp",EDGE,"E44")}),-1.0]])]}),sQuery(id+"F35.wireOp",EDGE,"E49"),sQuery(id+"F36.wireOp",EDGE,"E55"),sQuery(id+"F37.wireOp",EDGE,"E60"),sQuery(id+"F38.wireOp",EDGE,"E65"),sQuery(id+"F39.wireOp",EDGE,"E70"),sQuery(id+"F40.wireOp",EDGE,"E75"),makeQuery(id+"F42.imprint","IMPRINT",FACE,{"disambiguationData":[TD([[makeQuery(id+"F42.imprint","IMPRINT",EDGE,{"derivedFrom":sQuery(id+"F42.wireOp",EDGE,"E77")}),1.0]])]})])]});
            var Q1;
            Q1=qCreatedBy(makeId("Front.planeOp"),FACE);
            mirror(context, id + "F46", {"entities" : qUnion([Q0]), "mirrorPlane" : qUnion([Q1])});
        }
        {
            var Q0;
            Q0=makeQuery(id+"F43.opLoft","SWEPT_BODY",BODY,{"disambiguationData":[OSD([makeQuery(id+"F34.imprint","IMPRINT",FACE,{"disambiguationData":[TD([[makeQuery(id+"F34.imprint","IMPRINT",EDGE,{"derivedFrom":sQuery(id+"F34.wireOp",EDGE,"E44")}),-1.0]])]}),sQuery(id+"F35.wireOp",EDGE,"E49"),sQuery(id+"F36.wireOp",EDGE,"E55"),sQuery(id+"F37.wireOp",EDGE,"E60"),sQuery(id+"F38.wireOp",EDGE,"E65"),sQuery(id+"F39.wireOp",EDGE,"E70"),sQuery(id+"F40.wireOp",EDGE,"E75"),makeQuery(id+"F42.imprint","IMPRINT",FACE,{"disambiguationData":[TD([[makeQuery(id+"F42.imprint","IMPRINT",EDGE,{"derivedFrom":sQuery(id+"F42.wireOp",EDGE,"E77")}),1.0]])]})])]});
            var Q1;
            Q1=makeQuery(id+"F24.opLoft","SWEPT_BODY",BODY,{"disambiguationData":[OSD([sQuery(id+"F0.wireOp",EDGE,"E0"),sQuery(id+"F0.wireOp",EDGE,"E1"),makeQuery(id+"F2.imprint","IMPRINT",FACE,{"disambiguationData":[TD([[makeQuery(id+"F2.imprint","IMPRINT",EDGE,{"derivedFrom":sQuery(id+"F2.wireOp",EDGE,"E17")}),1.0]])]}),sQuery(id+"F4.wireOp",EDGE,"20f9a9d6-bc65-4b56-93dc-246f9f7381e10.MirrorCS"),sQuery(id+"F6.wireOp",EDGE,"0707af4e-3cc8-41db-9e1f-9e994c5d80550.MirrorCS"),sQuery(id+"F8.wireOp",EDGE,"e204524c-ed03-468d-9b7a-d2529ba048e80.MirrorCS"),sQuery(id+"F10.wireOp",EDGE,"80e8f1ac-6b9f-4b88-b722-8bd61400b4310.MirrorCS"),sQuery(id+"F12.wireOp",EDGE,"ef2bf6a3-3cea-4adc-a7b9-6d65ff93d0b10.MirrorCS"),sQuery(id+"F14.wireOp",EDGE,"f8b2d4a7-3851-43f8-8b17-44200d4f473c0.MirrorCS"),sQuery(id+"F16.wireOp",EDGE,"E31.MirrorCS"),sQuery(id+"F18.wireOp",EDGE,"E34.MirrorCS"),sQuery(id+"F20.wireOp",EDGE,"E35"),makeQuery(id+"F22.imprint","IMPRINT",FACE,{"disambiguationData":[TD([[makeQuery(id+"F22.imprint","IMPRINT",EDGE,{"derivedFrom":sQuery(id+"F22.wireOp",EDGE,"E37")}),1.0]])]})])]});
            var Q2;
            Q2=makeQuery(id+"F46.opPattern","COPY",BODY,{"derivedFrom":makeQuery(id+"F43.opLoft","SWEPT_BODY",BODY,{"disambiguationData":[OSD([makeQuery(id+"F34.imprint","IMPRINT",FACE,{"disambiguationData":[TD([[makeQuery(id+"F34.imprint","IMPRINT",EDGE,{"derivedFrom":sQuery(id+"F34.wireOp",EDGE,"E44")}),-1.0]])]}),sQuery(id+"F35.wireOp",EDGE,"E49"),sQuery(id+"F36.wireOp",EDGE,"E55"),sQuery(id+"F37.wireOp",EDGE,"E60"),sQuery(id+"F38.wireOp",EDGE,"E65"),sQuery(id+"F39.wireOp",EDGE,"E70"),sQuery(id+"F40.wireOp",EDGE,"E75"),makeQuery(id+"F42.imprint","IMPRINT",FACE,{"disambiguationData":[TD([[makeQuery(id+"F42.imprint","IMPRINT",EDGE,{"derivedFrom":sQuery(id+"F42.wireOp",EDGE,"E77")}),1.0]])]})])]}),"instanceName":"1"});
            booleanBodies(context, id + "F47", {"operationType" : BooleanOperationType.UNION, "tools" : qUnion([Q0, Q1, Q2])});
        }
        {
            var Q0;
            Q0=makeQuery(id+"F47.opBoolean","INTERSECT",EDGE,{"derivedFrom":[makeQuery(id+"F24.opLoft","SWEPT_FACE",FACE,{"disambiguationData":[OSD([sQuery(id+"F0.wireOp",EDGE,"E0"),sQuery(id+"F0.wireOp",EDGE,"E1"),sQuery(id+"F2.wireOp",EDGE,"E17"),sQuery(id+"F2.wireOp",EDGE,"E18.MirrorCS"),sQuery(id+"F4.wireOp",EDGE,"E19"),sQuery(id+"F4.wireOp",EDGE,"E20.MirrorCS")])]}),makeQuery(id+"F43.opLoft","SWEPT_FACE",FACE,{"disambiguationData":[OSD([sQuery(id+"F34.wireOp",EDGE,"E44"),sQuery(id+"F35.wireOp",EDGE,"E49"),sQuery(id+"F36.wireOp",EDGE,"E55"),sQuery(id+"F37.wireOp",EDGE,"E60"),sQuery(id+"F38.wireOp",EDGE,"E65"),sQuery(id+"F39.wireOp",EDGE,"E70"),sQuery(id+"F40.wireOp",EDGE,"E75"),sQuery(id+"F42.wireOp",EDGE,"E77")])]})]});
            var Q1;
            Q1=makeQuery(id+"F47.opBoolean","INTERSECT",EDGE,{"derivedFrom":[makeQuery(id+"F24.opLoft","SWEPT_FACE",FACE,{"disambiguationData":[OSD([sQuery(id+"F0.wireOp",EDGE,"E0"),sQuery(id+"F0.wireOp",EDGE,"E1"),sQuery(id+"F2.wireOp",EDGE,"E18.MirrorCS"),sQuery(id+"F4.wireOp",EDGE,"E20.MirrorCS")])]}),makeQuery(id+"F46.opPattern","COPY",FACE,{"derivedFrom":makeQuery(id+"F43.opLoft","SWEPT_FACE",FACE,{"disambiguationData":[OSD([sQuery(id+"F34.wireOp",EDGE,"E44"),sQuery(id+"F35.wireOp",EDGE,"E49"),sQuery(id+"F36.wireOp",EDGE,"E55"),sQuery(id+"F37.wireOp",EDGE,"E60"),sQuery(id+"F38.wireOp",EDGE,"E65"),sQuery(id+"F39.wireOp",EDGE,"E70"),sQuery(id+"F40.wireOp",EDGE,"E75"),sQuery(id+"F42.wireOp",EDGE,"E77")])]}),"instanceName":"1"})]});
            fillet(context, id + "F48", {"entities" : qUnion([Q0, Q1]), "radius" : 6 * mm, "tangentPropagation" : true, "allowEdgeOverflow" : false});
        }
        {
            var Q0;
            Q0=qCreatedBy(makeId("Top.planeOp"),FACE);
            var sketch = newSketch(context, id + "F49", { "sketchPlane" : qUnion([Q0])});
            skArc(sketch, "E78", {"start": v(-108.57, 52.64) * mm, "mid": v(-131.3, 0) * mm, "end": v(-108.57, -52.64) * mm});
            skLineSegment(sketch, "E79", {"start": v(-58.98, 0) * mm, "end": v(-108.57, -52.64) * mm, "construction": true});
            skLineSegment(sketch, "E80", {"start": v(-58.98, 0) * mm, "end": v(-131.3, 0) * mm, "construction": true});
            skLineSegment(sketch, "E81.MirrorCS", {"start": v(-58.98, 0) * mm, "end": v(-108.57, 52.64) * mm, "construction": true});
            skLineSegment(sketch, "E82", {"start": v(-108.57, -52.64) * mm, "end": v(-142.5, -52.64) * mm});
            skLineSegment(sketch, "E83", {"start": v(-108.57, 52.64) * mm, "end": v(-142.5, 52.64) * mm});
            skLineSegment(sketch, "E84", {"start": v(-142.5, 52.64) * mm, "end": v(-142.5, -52.64) * mm});
            skSolve(sketch);
        }
        {
            var Q0;
            Q0 = qSketchRegion(id + "F49", true);
            extrude(context, id + "F50", {"entities" : qUnion([Q0]), "operationType" : NewBodyOperationType.REMOVE, "depth" : 10 * mm});
        }
    });
